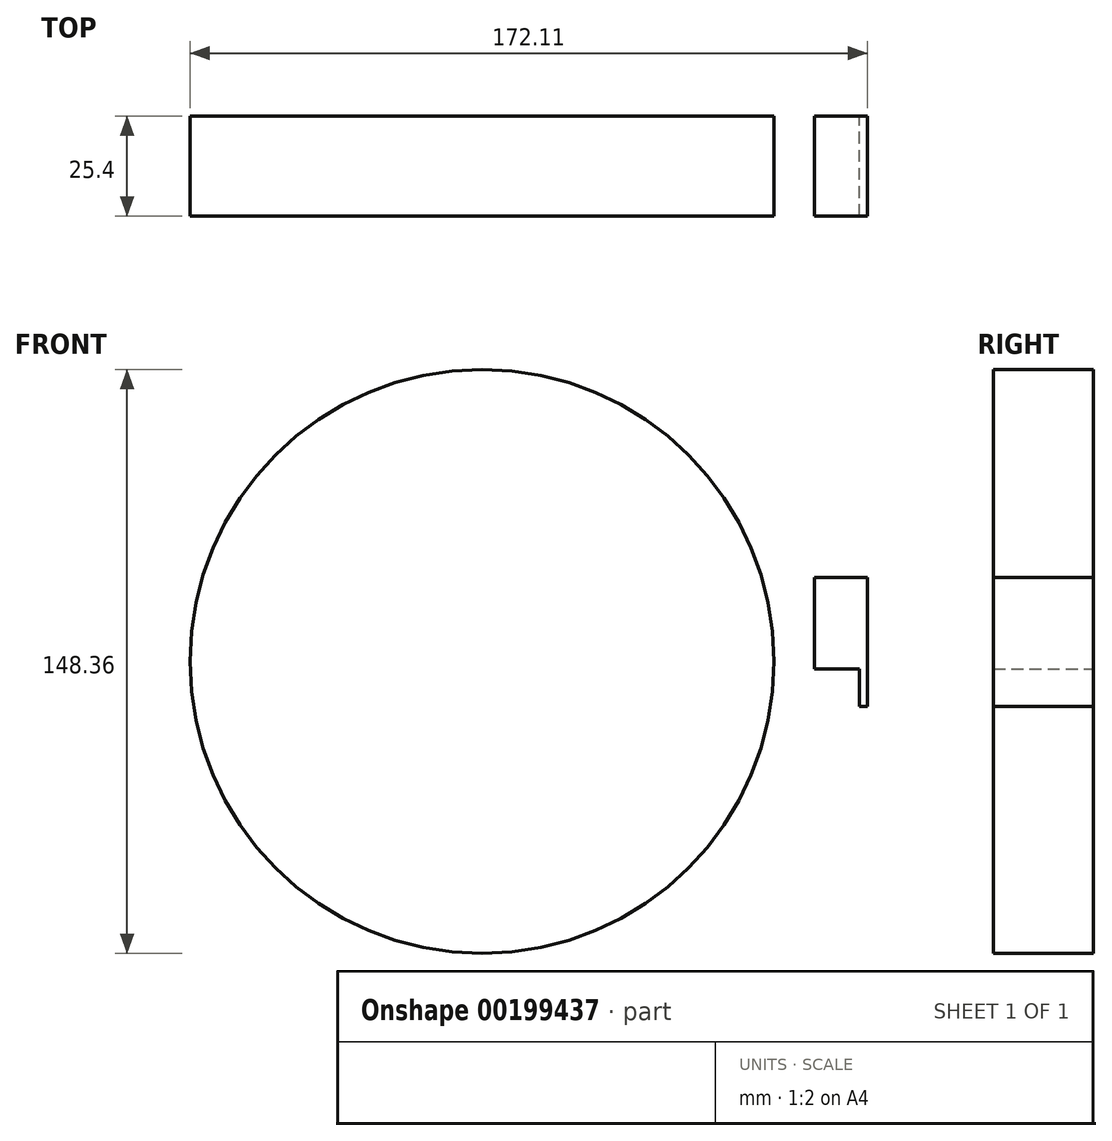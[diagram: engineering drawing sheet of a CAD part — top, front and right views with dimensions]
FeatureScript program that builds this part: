
annotation { "Feature Type Name" : "Feature", "Feature Type Description" : "" }
export const myFeature = defineFeature(function(context is Context, id is Id, definition is map)
    precondition{}
    {
        {
            var Q0;
            Q0=qCreatedBy(makeId("Front.planeOp"),FACE);
            var sketch = newSketch(context, id + "F0", { "sketchPlane" : qUnion([Q0])});
            skCircle(sketch, "E0", {"center": v(0, 0) * mm, "radius": 9.26 * mm});
            skCircle(sketch, "E1", {"center": v(0, 0) * mm, "radius": 2.97 * mm});
            skCircle(sketch, "E2", {"center": v(0, 0) * mm, "radius": 6.76 * mm});
            skCircle(sketch, "E3", {"center": v(0, 0) * mm, "radius": 13.18 * mm});
            skCircle(sketch, "E4", {"center": v(0, 0) * mm, "radius": 17.46 * mm});
            skCircle(sketch, "E5", {"center": v(0, 0) * mm, "radius": 23.22 * mm});
            skCircle(sketch, "E6", {"center": v(0, 0) * mm, "radius": 30.88 * mm});
            skCircle(sketch, "E7", {"center": v(0, 0) * mm, "radius": 40.32 * mm});
            skCircle(sketch, "E8", {"center": v(0, 0) * mm, "radius": 53.22 * mm});
            skCircle(sketch, "E9", {"center": v(0, 0) * mm, "radius": 74.18 * mm});
            skCircle(sketch, "E10", {"center": v(0, 0) * mm, "radius": 5.06 * mm});
            skLineSegment(sketch, "E11", {"start": v(0, 0) * mm, "end": v(-40.3, -79.65) * mm});
            skLineSegment(sketch, "E12", {"start": v(-40.3, -79.65) * mm, "end": v(-54.95, -86.98) * mm});
            skLineSegment(sketch, "E13", {"start": v(-54.95, -86.98) * mm, "end": v(-40.3, -79.65) * mm});
            skLineSegment(sketch, "E14", {"start": v(-40.3, -94.68) * mm, "end": v(-40.3, -79.65) * mm});
            skLineSegment(sketch, "E15", {"start": v(-40.3, -79.65) * mm, "end": v(-48.66, -91.44) * mm});
            skLineSegment(sketch, "E16", {"start": v(0, 0) * mm, "end": v(0.81, -2.69) * mm});
            skLineSegment(sketch, "E17", {"start": v(0, 0) * mm, "end": v(-2.52, -1.24) * mm});
            skLineSegment(sketch, "E18.bottom", {"start": v(-93.23, 39.73) * mm, "end": v(-108.89, 39.73) * mm});
            skLineSegment(sketch, "E18.top", {"start": v(-93.23, 54.48) * mm, "end": v(-108.89, 54.48) * mm});
            skLineSegment(sketch, "E18.left", {"start": v(-93.23, 39.73) * mm, "end": v(-93.23, 54.48) * mm});
            skLineSegment(sketch, "E18.right", {"start": v(-108.89, 39.73) * mm, "end": v(-108.89, 54.48) * mm});
            skPoint(sketch, "E18.middle", {"position": v(-101.06, 47.1) * mm});
            skLineSegment(sketch, "E19.bottom", {"start": v(-87.2, 22.5) * mm, "end": v(-109.56, 22.5) * mm});
            skLineSegment(sketch, "E19.top", {"start": v(-87.2, -30.7) * mm, "end": v(-109.56, -30.7) * mm});
            skLineSegment(sketch, "E19.left", {"start": v(-87.2, 22.5) * mm, "end": v(-87.2, -30.7) * mm});
            skLineSegment(sketch, "E19.right", {"start": v(-109.56, 22.5) * mm, "end": v(-109.56, -30.7) * mm});
            skPoint(sketch, "E19.middle", {"position": v(-98.38, -4.1) * mm});
            skLineSegment(sketch, "E20.bottom", {"start": v(-95.02, 5.74) * mm, "end": v(-86.53, 5.74) * mm});
            skLineSegment(sketch, "E20.top", {"start": v(-95.02, 59.4) * mm, "end": v(-86.53, 59.4) * mm});
            skLineSegment(sketch, "E20.left", {"start": v(-95.02, 5.74) * mm, "end": v(-95.02, 59.4) * mm});
            skLineSegment(sketch, "E20.right", {"start": v(-86.53, 5.74) * mm, "end": v(-86.53, 59.4) * mm});
            skPoint(sketch, "E20.middle", {"position": v(-90.78, 32.57) * mm});
            skLineSegment(sketch, "E21.bottom", {"start": v(-104.41, 19.38) * mm, "end": v(-92.34, 19.38) * mm});
            skLineSegment(sketch, "E21.top", {"start": v(-104.41, 44.42) * mm, "end": v(-92.34, 44.42) * mm});
            skLineSegment(sketch, "E21.left", {"start": v(-104.41, 19.38) * mm, "end": v(-104.41, 44.42) * mm});
            skLineSegment(sketch, "E21.right", {"start": v(-92.34, 19.38) * mm, "end": v(-92.34, 44.42) * mm});
            skPoint(sketch, "E21.middle", {"position": v(-98.38, 31.9) * mm});
            skLineSegment(sketch, "E22.bottom", {"start": v(81.16, -71.4) * mm, "end": v(103.07, -71.4) * mm});
            skLineSegment(sketch, "E22.top", {"start": v(81.16, -32.5) * mm, "end": v(103.07, -32.5) * mm});
            skLineSegment(sketch, "E22.left", {"start": v(81.16, -71.4) * mm, "end": v(81.16, -32.5) * mm});
            skLineSegment(sketch, "E22.right", {"start": v(103.07, -71.4) * mm, "end": v(103.07, -32.5) * mm});
            skLineSegment(sketch, "E23.bottom", {"start": v(81.16, -32.5) * mm, "end": v(95.92, -32.5) * mm});
            skLineSegment(sketch, "E23.top", {"start": v(81.16, -1.86) * mm, "end": v(95.92, -1.86) * mm});
            skLineSegment(sketch, "E23.left", {"start": v(81.16, -32.5) * mm, "end": v(81.16, -1.86) * mm});
            skLineSegment(sketch, "E23.right", {"start": v(95.92, -32.5) * mm, "end": v(95.92, -1.86) * mm});
            skLineSegment(sketch, "E24.bottom", {"start": v(100.39, -32.5) * mm, "end": v(95.92, -32.5) * mm});
            skLineSegment(sketch, "E24.top", {"start": v(100.39, -11.48) * mm, "end": v(95.92, -11.48) * mm});
            skLineSegment(sketch, "E24.left", {"start": v(100.39, -32.5) * mm, "end": v(100.39, -11.48) * mm});
            skLineSegment(sketch, "E24.right", {"start": v(95.92, -32.5) * mm, "end": v(95.92, -11.48) * mm});
            skLineSegment(sketch, "E25.bottom", {"start": v(100.39, -11.48) * mm, "end": v(97.93, -11.48) * mm});
            skLineSegment(sketch, "E25.top", {"start": v(100.39, 16.25) * mm, "end": v(97.93, 16.25) * mm});
            skLineSegment(sketch, "E25.left", {"start": v(100.39, -11.48) * mm, "end": v(100.39, 16.25) * mm});
            skLineSegment(sketch, "E25.right", {"start": v(97.93, -11.48) * mm, "end": v(97.93, 16.25) * mm});
            skLineSegment(sketch, "E26.bottom", {"start": v(84.52, -1.86) * mm, "end": v(97.93, -1.86) * mm});
            skLineSegment(sketch, "E26.top", {"start": v(84.52, 21.4) * mm, "end": v(97.93, 21.4) * mm});
            skLineSegment(sketch, "E26.left", {"start": v(84.52, -1.86) * mm, "end": v(84.52, 21.4) * mm});
            skLineSegment(sketch, "E26.right", {"start": v(97.93, -1.86) * mm, "end": v(97.93, 21.4) * mm});
            skPoint(sketch, "E27.oppositeSnap0", {"position": v(97.93, 2.39) * mm});
            skLineSegment(sketch, "E27.bottom", {"start": v(87.87, 21.4) * mm, "end": v(97.93, 21.4) * mm});
            skLineSegment(sketch, "E27.top", {"start": v(87.87, 39.5) * mm, "end": v(97.93, 39.5) * mm});
            skLineSegment(sketch, "E27.left", {"start": v(87.87, 21.4) * mm, "end": v(87.87, 39.5) * mm});
            skLineSegment(sketch, "E27.right", {"start": v(97.93, 21.4) * mm, "end": v(97.93, 39.5) * mm});
            skLineSegment(sketch, "E28", {"start": v(92.9, 39.5) * mm, "end": v(92.9, 63.87) * mm});
            skLineSegment(sketch, "E29", {"start": v(95.92, 39.5) * mm, "end": v(95.92, 48.45) * mm});
            skLineSegment(sketch, "E30", {"start": v(90.1, 39.5) * mm, "end": v(90.1, 53.59) * mm});
            skLineSegment(sketch, "E31.bottom", {"start": v(-1773.6, 1218.3) * mm, "end": v(-1351.97, 1218.3) * mm});
            skLineSegment(sketch, "E31.top", {"start": v(-1773.6, 917.14) * mm, "end": v(-1351.97, 917.14) * mm});
            skLineSegment(sketch, "E31.left", {"start": v(-1773.6, 1218.3) * mm, "end": v(-1773.6, 917.14) * mm});
            skLineSegment(sketch, "E31.right", {"start": v(-1351.97, 1218.3) * mm, "end": v(-1351.97, 917.14) * mm});
            skSolve(sketch);
        }
        {
            var Q0;
            Q0=makeQuery(id+"F0.imprint","IMPRINT",FACE,{"disambiguationData":[TD([[makeQuery(id+"F0.imprint","IMPRINT",EDGE,{"derivedFrom":sQuery(id+"F0.wireOp",EDGE,"E8")}),-1.0]])]});
            var Q1;
            Q1=makeQuery(id+"F0.imprint","IMPRINT",FACE,{"disambiguationData":[TD([[makeQuery(id+"F0.imprint","IMPRINT",EDGE,{"derivedFrom":sQuery(id+"F0.wireOp",EDGE,"E22.bottom")}),1.0]])]});
            var Q2;
            Q2=makeQuery(id+"F0.imprint","IMPRINT",FACE,{"disambiguationData":[TD([[makeQuery(id+"F0.imprint","IMPRINT",EDGE,{"derivedFrom":sQuery(id+"F0.wireOp",EDGE,"E7")}),-1.0]])]});
            var Q3;
            Q3=makeQuery(id+"F0.imprint","IMPRINT",FACE,{"disambiguationData":[TD([[makeQuery(id+"F0.imprint","IMPRINT",EDGE,{"derivedFrom":sQuery(id+"F0.wireOp",EDGE,"E6")}),-1.0]])]});
            var Q4;
            Q4=makeQuery(id+"F0.imprint","IMPRINT",FACE,{"disambiguationData":[TD([[makeQuery(id+"F0.imprint","IMPRINT",EDGE,{"derivedFrom":sQuery(id+"F0.wireOp",EDGE,"E5")}),-1.0]])]});
            var Q5;
            Q5=makeQuery(id+"F0.imprint","IMPRINT",FACE,{"disambiguationData":[TD([[makeQuery(id+"F0.imprint","IMPRINT",EDGE,{"derivedFrom":sQuery(id+"F0.wireOp",EDGE,"E4")}),-1.0]])]});
            var Q6;
            Q6=makeQuery(id+"F0.imprint","IMPRINT",FACE,{"disambiguationData":[TD([[makeQuery(id+"F0.imprint","IMPRINT",EDGE,{"derivedFrom":sQuery(id+"F0.wireOp",EDGE,"E3")}),-1.0]])]});
            var Q7;
            {var subQ2=sQuery(id+"F0.wireOp",EDGE,"E19.top");Q7=makeQuery(id+"F0.imprint","IMPRINT",FACE,{"disambiguationData":[TD([[makeQuery(id+"F0.imprint","IMPRINT",EDGE,{"derivedFrom":subQ2}),-1.0]])]});}
            var Q8;
            Q8=makeQuery(id+"F0.imprint","IMPRINT",FACE,{"disambiguationData":[TD([[makeQuery(id+"F0.imprint","IMPRINT",EDGE,{"derivedFrom":sQuery(id+"F0.wireOp",EDGE,"E0")}),-1.0]])]});
            var Q9;
            Q9=makeQuery(id+"F0.imprint","IMPRINT",FACE,{"disambiguationData":[TD([[makeQuery(id+"F0.imprint","IMPRINT",EDGE,{"derivedFrom":sQuery(id+"F0.wireOp",EDGE,"E23.bottom")}),1.0]])]});
            var Q10;
            {var subQ0=sQuery(id+"F0.wireOp",EDGE,"E21.left");var subQ1=sQuery(id+"F0.wireOp",EDGE,"E18.bottom");var subQ2=makeQuery(id+"F0.imprint","INTERSECT",VERTEX,{"derivedFrom":[subQ1,subQ0]});Q10=makeQuery(id+"F0.imprint","IMPRINT",FACE,{"disambiguationData":[TD([[makeQuery(id+"F0.imprint","IMPRINT",EDGE,{"disambiguationData":[TD([[subQ2,1.0]])],"derivedFrom":subQ1}),-1.0]])]});}
            var Q11;
            Q11=makeQuery(id+"F0.imprint","IMPRINT",FACE,{"disambiguationData":[TD([[makeQuery(id+"F0.imprint","IMPRINT",EDGE,{"derivedFrom":sQuery(id+"F0.wireOp",EDGE,"E26.top")}),-1.0]])]});
            var Q12;
            {var subQ5=sQuery(id+"F0.wireOp",EDGE,"E19.left");var subQ7=sQuery(id+"F0.wireOp",EDGE,"E19.bottom");var subQ8=makeQuery(id+"F0.imprint","INTERSECT",VERTEX,{"derivedFrom":[subQ7,subQ5]});Q12=makeQuery(id+"F0.imprint","IMPRINT",FACE,{"disambiguationData":[TD([[makeQuery(id+"F0.imprint","IMPRINT",EDGE,{"disambiguationData":[TD([[subQ8,-1.0]])],"derivedFrom":subQ7}),1.0]])]});}
            var Q13;
            {var subQ5=sQuery(id+"F0.wireOp",EDGE,"E18.right");Q13=makeQuery(id+"F0.imprint","IMPRINT",FACE,{"disambiguationData":[TD([[makeQuery(id+"F0.imprint","IMPRINT",EDGE,{"derivedFrom":subQ5}),-1.0]])]});}
            var Q14;
            {var subQ16=sQuery(id+"F0.wireOp",EDGE,"E20.top");Q14=makeQuery(id+"F0.imprint","IMPRINT",FACE,{"disambiguationData":[TD([[makeQuery(id+"F0.imprint","IMPRINT",EDGE,{"derivedFrom":subQ16}),-1.0]])]});}
            var Q15;
            {var subQ0=sQuery(id+"F0.wireOp",EDGE,"E21.left");var subQ1=sQuery(id+"F0.wireOp",EDGE,"E18.bottom");var subQ2=makeQuery(id+"F0.imprint","INTERSECT",VERTEX,{"derivedFrom":[subQ1,subQ0]});Q15=makeQuery(id+"F0.imprint","IMPRINT",FACE,{"disambiguationData":[TD([[makeQuery(id+"F0.imprint","IMPRINT",EDGE,{"disambiguationData":[TD([[subQ2,1.0]])],"derivedFrom":subQ1}),1.0]])]});}
            var Q16;
            Q16=makeQuery(id+"F0.imprint","IMPRINT",FACE,{"disambiguationData":[TD([[makeQuery(id+"F0.imprint","IMPRINT",EDGE,{"derivedFrom":sQuery(id+"F0.wireOp",EDGE,"E27.bottom")}),1.0]])]});
            var Q17;
            {var subQ0=sQuery(id+"F0.wireOp",EDGE,"E21.right");var subQ1=sQuery(id+"F0.wireOp",EDGE,"E19.bottom");var subQ2=makeQuery(id+"F0.imprint","INTERSECT",VERTEX,{"derivedFrom":[subQ1,subQ0]});Q17=makeQuery(id+"F0.imprint","IMPRINT",FACE,{"disambiguationData":[TD([[makeQuery(id+"F0.imprint","IMPRINT",EDGE,{"disambiguationData":[TD([[subQ2,-1.0]])],"derivedFrom":subQ1}),1.0]])]});}
            var Q18;
            {var subQ0=sQuery(id+"F0.wireOp",EDGE,"E21.left");var subQ1=sQuery(id+"F0.wireOp",EDGE,"E19.bottom");var subQ2=makeQuery(id+"F0.imprint","INTERSECT",VERTEX,{"derivedFrom":[subQ1,subQ0]});Q18=makeQuery(id+"F0.imprint","IMPRINT",FACE,{"disambiguationData":[TD([[makeQuery(id+"F0.imprint","IMPRINT",EDGE,{"disambiguationData":[TD([[subQ2,1.0]])],"derivedFrom":subQ1}),1.0]])]});}
            var Q19;
            {var subQ0=sQuery(id+"F0.wireOp",EDGE,"E18.left");var subQ1=sQuery(id+"F0.wireOp",EDGE,"E18.bottom");var subQ2=makeQuery(id+"F0.imprint","INTERSECT",VERTEX,{"derivedFrom":[subQ1,subQ0]});Q19=makeQuery(id+"F0.imprint","IMPRINT",FACE,{"disambiguationData":[TD([[makeQuery(id+"F0.imprint","IMPRINT",EDGE,{"disambiguationData":[TD([[subQ2,-1.0]])],"derivedFrom":subQ1}),-1.0]])]});}
            var Q20;
            {var subQ0=sQuery(id+"F0.wireOp",EDGE,"E18.left");var subQ1=sQuery(id+"F0.wireOp",EDGE,"E18.top");var subQ2=makeQuery(id+"F0.imprint","INTERSECT",VERTEX,{"derivedFrom":[subQ1,subQ0]});Q20=makeQuery(id+"F0.imprint","IMPRINT",FACE,{"disambiguationData":[TD([[makeQuery(id+"F0.imprint","IMPRINT",EDGE,{"disambiguationData":[TD([[subQ2,-1.0]])],"derivedFrom":subQ1}),1.0]])]});}
            var Q21;
            {var subQ5=sQuery(id+"F0.wireOp",EDGE,"E18.bottom");var subQ9=sQuery(id+"F0.wireOp",EDGE,"E18.left");var subQ10=makeQuery(id+"F0.imprint","INTERSECT",VERTEX,{"derivedFrom":[subQ5,subQ9]});Q21=makeQuery(id+"F0.imprint","IMPRINT",FACE,{"disambiguationData":[TD([[makeQuery(id+"F0.imprint","IMPRINT",EDGE,{"disambiguationData":[TD([[subQ10,-1.0]])],"derivedFrom":subQ5}),1.0]])]});}
            var Q22;
            Q22=makeQuery(id+"F0.imprint","IMPRINT",FACE,{"disambiguationData":[TD([[makeQuery(id+"F0.imprint","IMPRINT",EDGE,{"derivedFrom":sQuery(id+"F0.wireOp",EDGE,"E25.bottom")}),-1.0]])]});
            var Q23;
            {var subQ0=sQuery(id+"F0.wireOp",EDGE,"E23.right");Q23=makeQuery(id+"F0.imprint","IMPRINT",FACE,{"disambiguationData":[TD([[makeQuery(id+"F0.imprint","IMPRINT",EDGE,{"derivedFrom":subQ0}),-1.0]])]});}
            var Q24;
            Q24=makeQuery(id+"F0.imprint","IMPRINT",FACE,{"disambiguationData":[TD([[makeQuery(id+"F0.imprint","IMPRINT",EDGE,{"derivedFrom":sQuery(id+"F0.wireOp",EDGE,"E24.bottom")}),-1.0]])]});
            var Q25;
            Q25=makeQuery(id+"F0.imprint","IMPRINT",FACE,{"disambiguationData":[TD([[makeQuery(id+"F0.imprint","IMPRINT",EDGE,{"derivedFrom":sQuery(id+"F0.wireOp",EDGE,"E0")}),1.0]])]});
            var Q26;
            Q26=makeQuery(id+"F0.imprint","IMPRINT",FACE,{"disambiguationData":[TD([[makeQuery(id+"F0.imprint","IMPRINT",EDGE,{"derivedFrom":sQuery(id+"F0.wireOp",EDGE,"E1")}),1.0]])]});
            var Q27;
            Q27=makeQuery(id+"F0.imprint","IMPRINT",FACE,{"disambiguationData":[TD([[makeQuery(id+"F0.imprint","IMPRINT",EDGE,{"derivedFrom":sQuery(id+"F0.wireOp",EDGE,"E2")}),1.0]])]});
            var Q28;
            Q28=makeQuery(id+"F0.imprint","IMPRINT",FACE,{"disambiguationData":[TD([[makeQuery(id+"F0.imprint","IMPRINT",EDGE,{"derivedFrom":sQuery(id+"F0.wireOp",EDGE,"E1")}),-1.0]])]});
            extrude(context, id + "F1", {"entities" : qUnion([Q0, Q1, Q2, Q3, Q4, Q5, Q6, Q7, Q8, Q9, Q10, Q11, Q12, Q13, Q14, Q15, Q16, Q17, Q18, Q19, Q20, Q21, Q22, Q23, Q24, Q25, Q26, Q27, Q28]), "depth" : 25.4 * mm});
        }
        {
            var Q0;
            Q0=makeQuery(id+"F1.opExtrude","SWEPT_BODY",BODY,{"disambiguationData":[OSD([sQuery(id+"F0.wireOp",EDGE,"E18.bottom"),sQuery(id+"F0.wireOp",EDGE,"E18.top"),sQuery(id+"F0.wireOp",EDGE,"E18.right"),sQuery(id+"F0.wireOp",EDGE,"E19.bottom"),sQuery(id+"F0.wireOp",EDGE,"E19.top"),sQuery(id+"F0.wireOp",EDGE,"E19.left"),sQuery(id+"F0.wireOp",EDGE,"E19.right"),sQuery(id+"F0.wireOp",EDGE,"E20.bottom"),sQuery(id+"F0.wireOp",EDGE,"E20.top"),sQuery(id+"F0.wireOp",EDGE,"E20.left"),sQuery(id+"F0.wireOp",EDGE,"E20.right"),sQuery(id+"F0.wireOp",EDGE,"E21.left")])]});
            deleteBodies(context, id + "F2", {"entities" : qUnion([Q0])});
        }
        {
            var Q0;
            Q0=makeQuery(id+"F1.opExtrude","SWEPT_BODY",BODY,{"disambiguationData":[OSD([sQuery(id+"F0.wireOp",EDGE,"E22.bottom"),sQuery(id+"F0.wireOp",EDGE,"E22.top"),sQuery(id+"F0.wireOp",EDGE,"E22.left"),sQuery(id+"F0.wireOp",EDGE,"E22.right"),sQuery(id+"F0.wireOp",EDGE,"E23.top"),sQuery(id+"F0.wireOp",EDGE,"E23.left"),sQuery(id+"F0.wireOp",EDGE,"E24.left"),sQuery(id+"F0.wireOp",EDGE,"E25.top"),sQuery(id+"F0.wireOp",EDGE,"E25.left"),sQuery(id+"F0.wireOp",EDGE,"E26.top"),sQuery(id+"F0.wireOp",EDGE,"E26.left"),sQuery(id+"F0.wireOp",EDGE,"E26.right"),sQuery(id+"F0.wireOp",EDGE,"E27.top"),sQuery(id+"F0.wireOp",EDGE,"E27.left"),sQuery(id+"F0.wireOp",EDGE,"E27.right")])]});
            deleteBodies(context, id + "F3", {"entities" : qUnion([Q0])});
        }
    });
